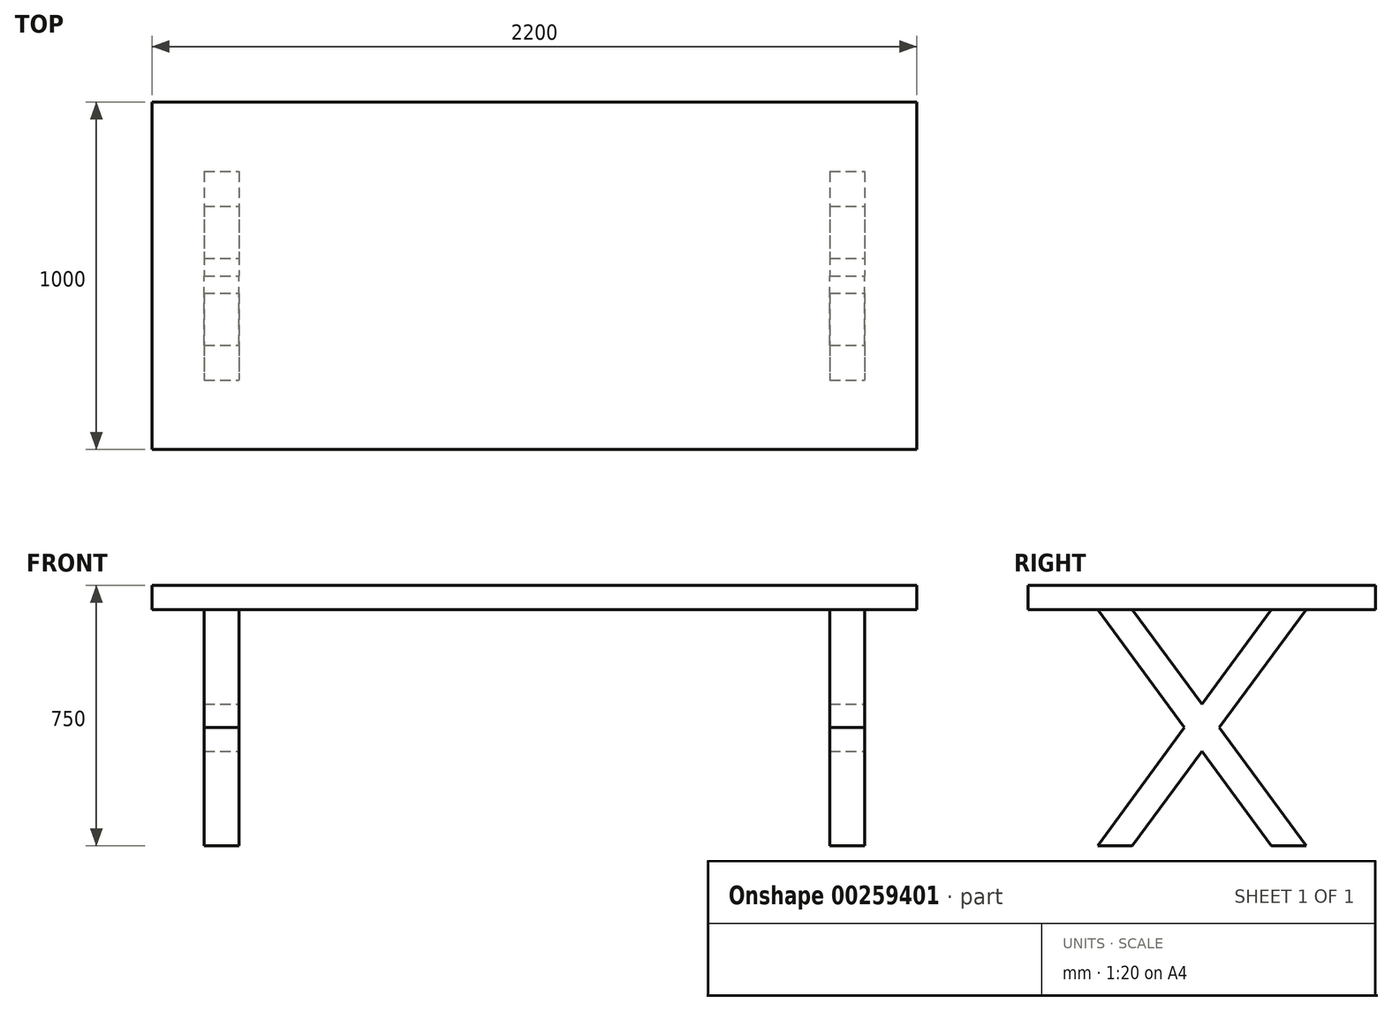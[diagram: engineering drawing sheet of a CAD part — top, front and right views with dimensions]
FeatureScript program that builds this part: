
annotation { "Feature Type Name" : "Feature", "Feature Type Description" : "" }
export const myFeature = defineFeature(function(context is Context, id is Id, definition is map)
    precondition{}
    {
        {
            var Q0;
            Q0=qCreatedBy(makeId("Top.planeOp"),FACE);
            var sketch = newSketch(context, id + "F0", { "sketchPlane" : qUnion([Q0])});
            skLineSegment(sketch, "E0.bottom", {"start": v(1100, 500) * mm, "end": v(-1100, 500) * mm});
            skLineSegment(sketch, "E0.top", {"start": v(1100, -500) * mm, "end": v(-1100, -500) * mm});
            skLineSegment(sketch, "E0.left", {"start": v(1100, 500) * mm, "end": v(1100, -500) * mm});
            skLineSegment(sketch, "E0.right", {"start": v(-1100, 500) * mm, "end": v(-1100, -500) * mm});
            skPoint(sketch, "E0.middle", {"position": v(0, 0) * mm});
            skSolve(sketch);
        }
        {
            var Q0;
            Q0=makeQuery(id+"F0.imprint","IMPRINT",FACE,{"disambiguationData":[TD([[makeQuery(id+"F0.imprint","IMPRINT",EDGE,{"derivedFrom":sQuery(id+"F0.wireOp",EDGE,"E0.bottom")}),1.0]])]});
            extrude(context, id + "F1", {"entities" : qUnion([Q0]), "oppositeDirection" : true, "depth" : 70 * mm});
        }
        {
            var Q0;
            Q0=makeQuery(id+"F1.opExtrude","SWEPT_FACE",FACE,{"disambiguationData":[OSD([sQuery(id+"F0.wireOp",EDGE,"E0.left")])]});
            var sketch = newSketch(context, id + "F2", { "sketchPlane" : qUnion([Q0])});
            skLineSegment(sketch, "E1.bottom", {"start": v(-500, -70) * mm, "end": v(500, -70) * mm});
            skLineSegment(sketch, "E1.top", {"start": v(-300, -750) * mm, "end": v(-200, -750) * mm});
            skLineSegment(sketch, "E1.right", {"start": v(500, -70) * mm, "end": v(500, -750) * mm});
            skLineSegment(sketch, "E2", {"start": v(-300, -70) * mm, "end": v(-50, -410) * mm});
            skLineSegment(sketch, "E3", {"start": v(-200, -70) * mm, "end": v(0, -342) * mm});
            skLineSegment(sketch, "E4.MirrorCS", {"start": v(200, -70) * mm, "end": v(0, -342) * mm});
            skLineSegment(sketch, "E5.MirrorCS", {"start": v(300, -70) * mm, "end": v(50, -410) * mm});
            skLineSegment(sketch, "E6.trimOffspring", {"start": v(50, -410) * mm, "end": v(300, -750) * mm});
            skLineSegment(sketch, "E7.trimOffspring", {"start": v(-50, -410) * mm, "end": v(-300, -750) * mm});
            skLineSegment(sketch, "E8.trimOffspring", {"start": v(0, -478) * mm, "end": v(200, -750) * mm});
            skLineSegment(sketch, "E9.trimOffspring", {"start": v(0, -478) * mm, "end": v(-200, -750) * mm});
            skLineSegment(sketch, "E10.trimOffspring", {"start": v(200, -750) * mm, "end": v(500, -750) * mm});
            skSolve(sketch);
        }
        {
            var Q0;
            Q0=makeQuery(id+"F2.imprint","IMPRINT",FACE,{"disambiguationData":[TD([[makeQuery(id+"F2.imprint","IMPRINT",EDGE,{"derivedFrom":sQuery(id+"F2.wireOp",EDGE,"E1.top")}),1.0]])]});
            var Q1;
            Q1=makeQuery(id+"F1.opExtrude","SWEPT_FACE",FACE,{"disambiguationData":[OSD([sQuery(id+"F0.wireOp",EDGE,"E0.right")])]});
            extrude(context, id + "F3", {"entities" : qUnion([Q0]), "operationType" : NewBodyOperationType.ADD, "endBound" : BoundingType.UP_TO_SURFACE, "oppositeDirection" : true, "endBoundEntityFace" : qUnion([Q1]), "depth" : 25 * mm});
        }
        {
            var Q0;
            Q0=makeQuery(id+"F1.opExtrude","SWEPT_FACE",FACE,{"disambiguationData":[OSD([sQuery(id+"F0.wireOp",EDGE,"E0.bottom")])]});
            var sketch = newSketch(context, id + "F4", { "sketchPlane" : qUnion([Q0])});
            skLineSegment(sketch, "E11.bottom", {"start": v(-1100, -70) * mm, "end": v(-950, -70) * mm});
            skLineSegment(sketch, "E11.top", {"start": v(-1100, -780.68) * mm, "end": v(-950, -780.68) * mm});
            skLineSegment(sketch, "E11.left", {"start": v(-1100, -70) * mm, "end": v(-1100, -780.68) * mm});
            skLineSegment(sketch, "E11.right", {"start": v(-950, -70) * mm, "end": v(-950, -780.68) * mm});
            skLineSegment(sketch, "E12.bottom", {"start": v(1100, -70) * mm, "end": v(950, -70) * mm});
            skLineSegment(sketch, "E12.top", {"start": v(1100, -827.2) * mm, "end": v(950, -827.2) * mm});
            skLineSegment(sketch, "E12.left", {"start": v(1100, -70) * mm, "end": v(1100, -827.2) * mm});
            skLineSegment(sketch, "E12.right", {"start": v(950, -70) * mm, "end": v(950, -827.2) * mm});
            skLineSegment(sketch, "E13.bottom", {"start": v(-850, -70) * mm, "end": v(850, -70) * mm});
            skLineSegment(sketch, "E13.top", {"start": v(-850, -831.93) * mm, "end": v(850, -831.93) * mm});
            skLineSegment(sketch, "E13.left", {"start": v(-850, -70) * mm, "end": v(-850, -831.93) * mm});
            skLineSegment(sketch, "E13.right", {"start": v(850, -70) * mm, "end": v(850, -831.93) * mm});
            skSolve(sketch);
        }
        {
            var Q0;
            Q0 = qSketchRegion(id + "F4", true);
            extrude(context, id + "F5", {"entities" : qUnion([Q0]), "operationType" : NewBodyOperationType.REMOVE, "endBound" : BoundingType.THROUGH_ALL, "oppositeDirection" : true, "depth" : 25 * mm});
        }
    });
